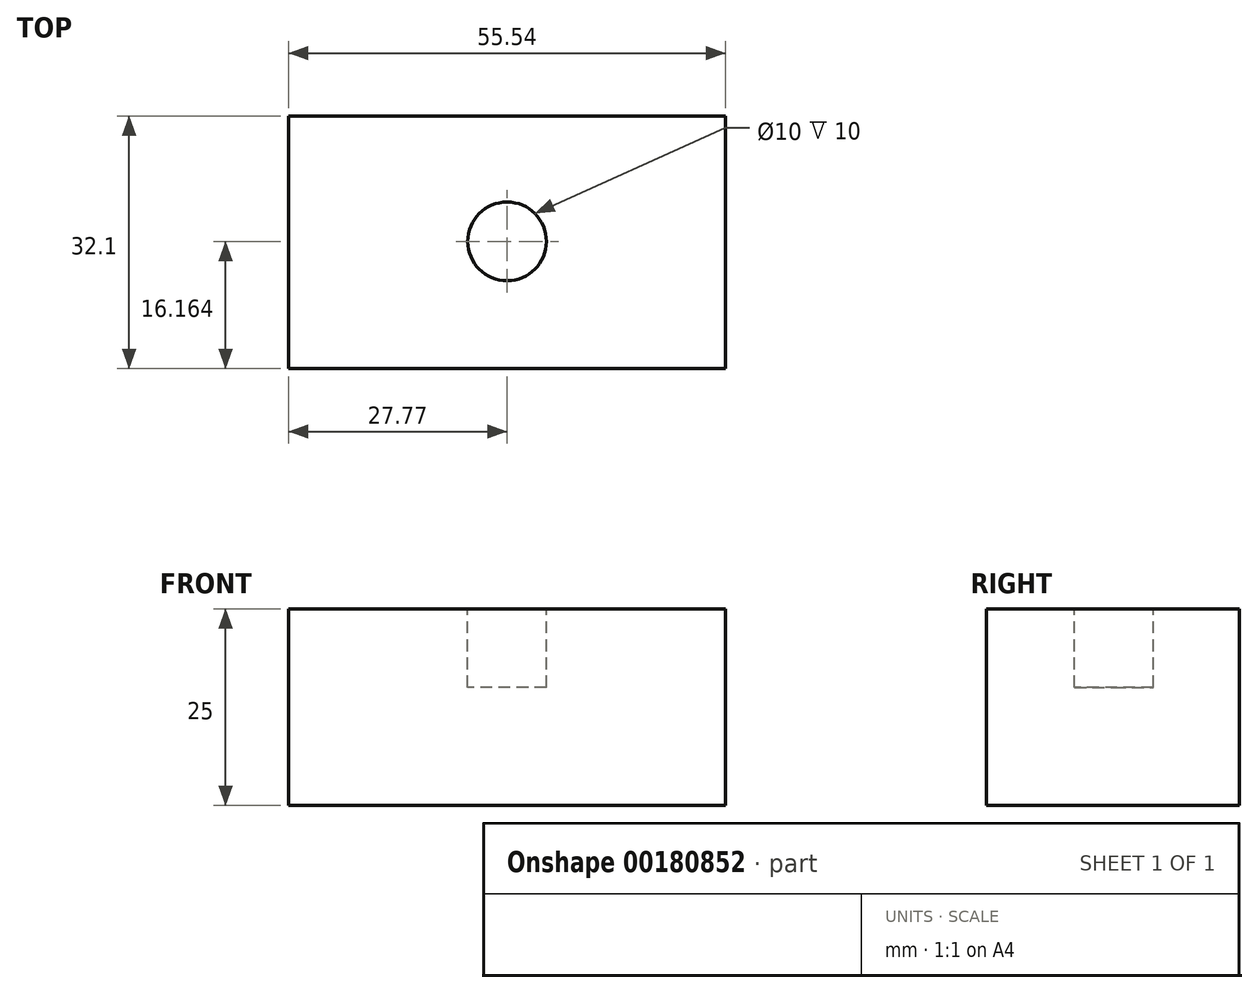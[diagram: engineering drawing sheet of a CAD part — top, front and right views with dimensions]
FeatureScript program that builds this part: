
annotation { "Feature Type Name" : "Feature", "Feature Type Description" : "" }
export const myFeature = defineFeature(function(context is Context, id is Id, definition is map)
    precondition{}
    {
        {
            var Q0;
            Q0=qCreatedBy(makeId("Top.planeOp"),FACE);
            var sketch = newSketch(context, id + "F0", { "sketchPlane" : qUnion([Q0])});
            skLineSegment(sketch, "E0.bottom", {"start": v(-27.77, 16.05) * mm, "end": v(27.77, 16.05) * mm});
            skLineSegment(sketch, "E0.top", {"start": v(-27.77, -16.05) * mm, "end": v(27.77, -16.05) * mm});
            skLineSegment(sketch, "E0.left", {"start": v(-27.77, 16.05) * mm, "end": v(-27.77, -16.05) * mm});
            skLineSegment(sketch, "E0.right", {"start": v(27.77, 16.05) * mm, "end": v(27.77, -16.05) * mm});
            skPoint(sketch, "E0.middle", {"position": v(0, 0) * mm});
            skSolve(sketch);
        }
        {
            var Q0;
            Q0=makeQuery(id+"F0.imprint","IMPRINT",FACE,{"disambiguationData":[TD([[makeQuery(id+"F0.imprint","IMPRINT",EDGE,{"derivedFrom":sQuery(id+"F0.wireOp",EDGE,"E0.bottom")}),-1.0]])]});
            extrude(context, id + "F1", {"entities" : qUnion([Q0]), "oppositeDirection" : true, "depth" : 25 * mm});
        }
        {
            var Q0;
            Q0=makeQuery(id+"F1.opExtrude","CAP_FACE",FACE,{"disambiguationData":[OSD([sQuery(id+"F0.wireOp",EDGE,"E0.bottom"),sQuery(id+"F0.wireOp",EDGE,"E0.top"),sQuery(id+"F0.wireOp",EDGE,"E0.left"),sQuery(id+"F0.wireOp",EDGE,"E0.right")])],"isStart":true});
            var sketch = newSketch(context, id + "F2", { "sketchPlane" : qUnion([Q0])});
            skArc(sketch, "E1", {"start": v(0, -4.89) * mm, "mid": v(5, 0.11) * mm, "end": v(0, 5.11) * mm});
            skArc(sketch, "E2", {"start": v(0, 5.11) * mm, "mid": v(-5, 0.11) * mm, "end": v(0, -4.89) * mm});
            skLineSegment(sketch, "E3", {"start": v(0, -4.89) * mm, "end": v(0, 5.11) * mm});
            skSolve(sketch);
        }
        {
            var Q0;
            Q0=makeQuery(id+"F2.imprint","IMPRINT",FACE,{"disambiguationData":[TD([[makeQuery(id+"F2.imprint","IMPRINT",EDGE,{"derivedFrom":sQuery(id+"F2.wireOp",EDGE,"E2")}),1.0]])]});
            extrude(context, id + "F3", {"entities" : qUnion([Q0]), "operationType" : NewBodyOperationType.REMOVE, "oppositeDirection" : true, "depth" : 10 * mm});
        }
        {
            var Q0;
            Q0=makeQuery(id+"F2.imprint","IMPRINT",FACE,{"disambiguationData":[TD([[makeQuery(id+"F2.imprint","IMPRINT",EDGE,{"derivedFrom":sQuery(id+"F2.wireOp",EDGE,"E1")}),1.0]])]});
            extrude(context, id + "F4", {"entities" : qUnion([Q0]), "operationType" : NewBodyOperationType.REMOVE, "oppositeDirection" : true, "depth" : 10 * mm});
        }
    });
